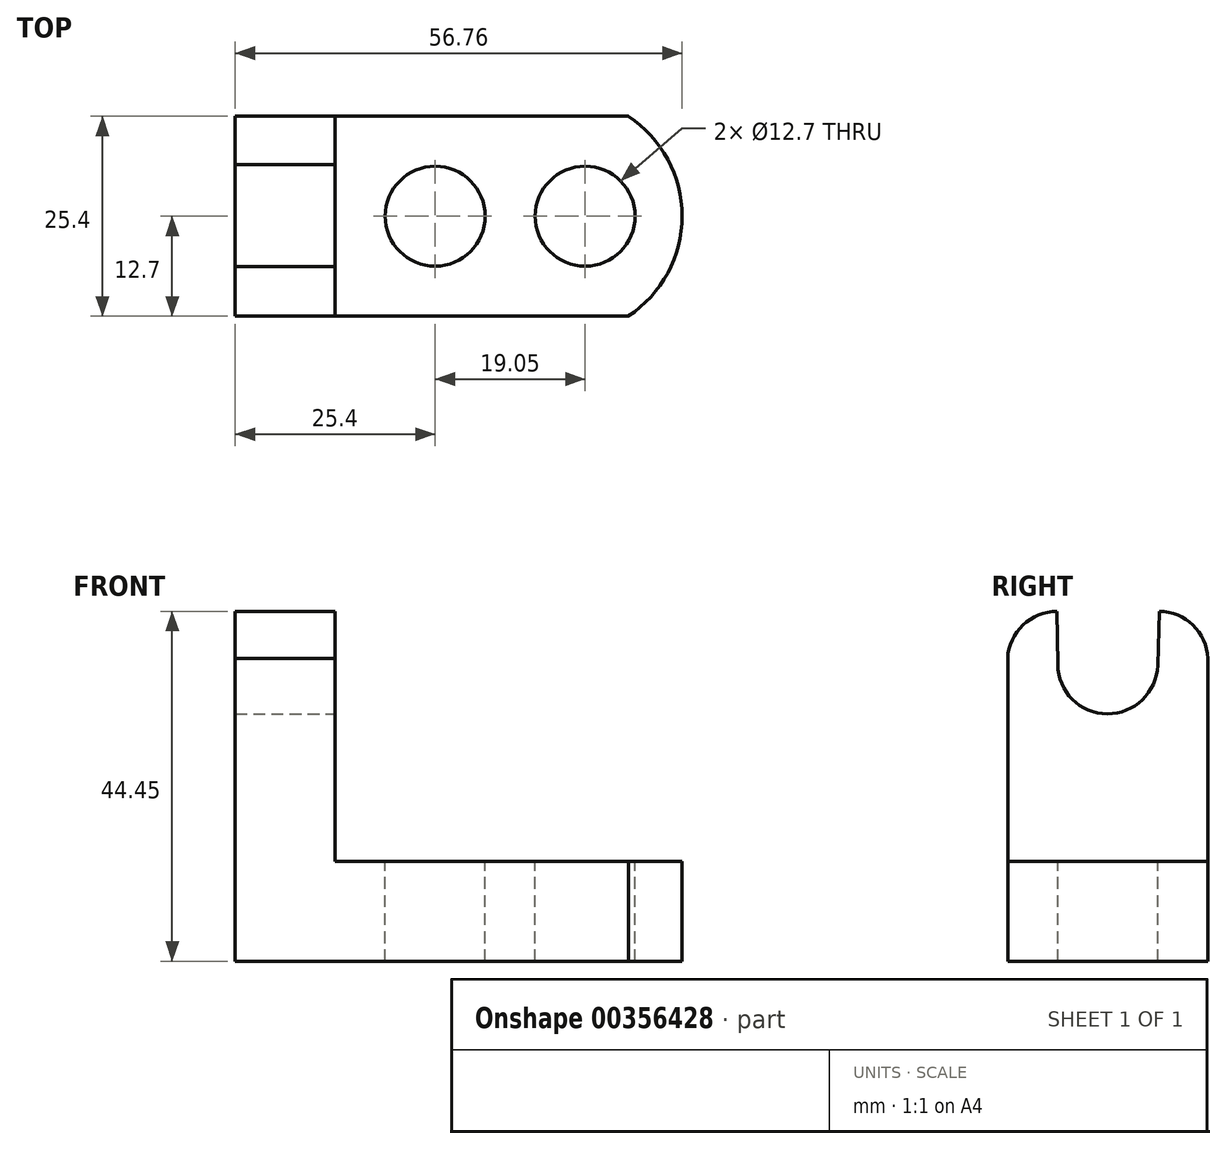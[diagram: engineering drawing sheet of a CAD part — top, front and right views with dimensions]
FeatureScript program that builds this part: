
annotation { "Feature Type Name" : "Feature", "Feature Type Description" : "" }
export const myFeature = defineFeature(function(context is Context, id is Id, definition is map)
    precondition{}
    {
        {
            var Q0;
            Q0=qCreatedBy(makeId("Front.planeOp"),FACE);
            var sketch = newSketch(context, id + "F0", { "sketchPlane" : qUnion([Q0])});
            skLineSegment(sketch, "E0", {"start": v(0, 44.45) * mm, "end": v(0, 0) * mm});
            skLineSegment(sketch, "E1", {"start": v(0, 0) * mm, "end": v(57.15, 0) * mm});
            skLineSegment(sketch, "E2", {"start": v(57.15, 0) * mm, "end": v(57.15, 44.45) * mm});
            skLineSegment(sketch, "E3", {"start": v(57.15, 44.45) * mm, "end": v(0, 44.45) * mm});
            skSolve(sketch);
        }
        {
            var Q0;
            Q0=makeQuery(id+"F0.imprint","IMPRINT",FACE,{"disambiguationData":[TD([[makeQuery(id+"F0.imprint","IMPRINT",EDGE,{"derivedFrom":sQuery(id+"F0.wireOp",EDGE,"E0")}),1.0]])]});
            extrude(context, id + "F1", {"entities" : qUnion([Q0]), "depth" : 25.4 * mm});
        }
        {
            var Q0;
            Q0=makeQuery(id+"F1.opExtrude","CAP_FACE",FACE,{"disambiguationData":[OSD([sQuery(id+"F0.wireOp",EDGE,"E0"),sQuery(id+"F0.wireOp",EDGE,"E1"),sQuery(id+"F0.wireOp",EDGE,"E2"),sQuery(id+"F0.wireOp",EDGE,"E3")])],"isStart":false});
            var sketch = newSketch(context, id + "F2", { "sketchPlane" : qUnion([Q0])});
            skLineSegment(sketch, "E4", {"start": v(12.7, 44.45) * mm, "end": v(12.7, 12.7) * mm});
            skLineSegment(sketch, "E5", {"start": v(12.7, 12.7) * mm, "end": v(57.15, 12.7) * mm});
            skSolve(sketch);
        }
        {
            var Q0;
            Q0 = qSketchRegion(id + "F2", true);
            var Q1;
            {var subQ0=sQuery(id+"F2.wireOp",EDGE,"E4");Q1=makeQuery(id+"F2.imprint","IMPRINT",FACE,{"disambiguationData":[TD([[makeQuery(id+"F2.imprint","IMPRINT",EDGE,{"derivedFrom":subQ0}),1.0]])]});}
            extrude(context, id + "F3", {"entities" : qUnion([Q0, Q1]), "operationType" : NewBodyOperationType.REMOVE, "oppositeDirection" : true, "depth" : 25.4 * mm});
        }
        {
            var Q0;
            Q0=makeQuery(id+"F3.boolean.opBoolean","COPY",FACE,{"derivedFrom":makeQuery(id+"F3.opExtrude","SWEPT_FACE",FACE,{"disambiguationData":[OSD([sQuery(id+"F2.wireOp",EDGE,"E4")])]})});
            var sketch = newSketch(context, id + "F4", { "sketchPlane" : qUnion([Q0])});
            skCircle(sketch, "E6", {"center": v(-12.7, 37.78) * mm, "radius": 6.35 * mm});
            skLineSegment(sketch, "E7", {"start": v(-19.05, 37.71) * mm, "end": v(-19.12, 44.45) * mm});
            skLineSegment(sketch, "E8", {"start": v(-19.12, 44.45) * mm, "end": v(-6.15, 44.45) * mm});
            skLineSegment(sketch, "E9", {"start": v(-6.15, 44.45) * mm, "end": v(-6.35, 37.6) * mm});
            skSolve(sketch);
        }
        {
            var Q0;
            {var subQ0=sQuery(id+"F4.wireOp",EDGE,"E7");Q0=makeQuery(id+"F4.imprint","IMPRINT",FACE,{"disambiguationData":[TD([[makeQuery(id+"F4.imprint","IMPRINT",EDGE,{"derivedFrom":subQ0}),-1.0]])]});}
            var Q1;
            {var subQ0=sQuery(id+"F4.wireOp",EDGE,"E6");var subQ1=makeQuery(id+"F4.imprint","INTERSECT",VERTEX,{"derivedFrom":[subQ0,sQuery(id+"F4.wireOp",EDGE,"E7")]});Q1=makeQuery(id+"F4.imprint","IMPRINT",FACE,{"disambiguationData":[TD([[makeQuery(id+"F4.imprint","IMPRINT",EDGE,{"disambiguationData":[TD([[subQ1,-1.0]])],"derivedFrom":subQ0}),1.0]])]});}
            extrude(context, id + "F5", {"entities" : qUnion([Q0, Q1]), "operationType" : NewBodyOperationType.REMOVE, "oppositeDirection" : true, "depth" : 25.4 * mm});
        }
        {
            var Q0;
            Q0=makeQuery(id+"F3.boolean.opBoolean","COPY",FACE,{"derivedFrom":makeQuery(id+"F3.opExtrude","SWEPT_FACE",FACE,{"disambiguationData":[OSD([sQuery(id+"F2.wireOp",EDGE,"E4")])]})});
            var sketch = newSketch(context, id + "F6", { "sketchPlane" : qUnion([Q0])});
            skArc(sketch, "E10", {"start": v(-19.12, 44.45) * mm, "mid": v(-23.46, 42.71) * mm, "end": v(-25.4, 38.47) * mm});
            skSolve(sketch);
        }
        {
            var Q0;
            Q0 = qSketchRegion(id + "F6", true);
            var Q1;
            {var subQ0=sQuery(id+"F6.wireOp",EDGE,"E10");Q1=makeQuery(id+"F6.imprint","IMPRINT",FACE,{"disambiguationData":[TD([[makeQuery(id+"F6.imprint","IMPRINT",EDGE,{"derivedFrom":subQ0}),-1.0]])]});}
            extrude(context, id + "F7", {"entities" : qUnion([Q0, Q1]), "operationType" : NewBodyOperationType.REMOVE, "oppositeDirection" : true, "depth" : 25.4 * mm});
        }
        {
            var Q0;
            Q0=makeQuery(id+"F3.boolean.opBoolean","COPY",FACE,{"derivedFrom":makeQuery(id+"F3.opExtrude","SWEPT_FACE",FACE,{"disambiguationData":[OSD([sQuery(id+"F2.wireOp",EDGE,"E4")])]})});
            var sketch = newSketch(context, id + "F8", { "sketchPlane" : qUnion([Q0])});
            skArc(sketch, "E11", {"start": v(0, 38.47) * mm, "mid": v(-1.86, 42.7) * mm, "end": v(-6.15, 44.45) * mm});
            skSolve(sketch);
        }
        {
            var Q0;
            Q0 = qSketchRegion(id + "F8", true);
            var Q1;
            {var subQ0=sQuery(id+"F8.wireOp",EDGE,"E11");Q1=makeQuery(id+"F8.imprint","IMPRINT",FACE,{"disambiguationData":[TD([[makeQuery(id+"F8.imprint","IMPRINT",EDGE,{"derivedFrom":subQ0}),-1.0]])]});}
            extrude(context, id + "F9", {"entities" : qUnion([Q0, Q1]), "operationType" : NewBodyOperationType.REMOVE, "oppositeDirection" : true, "depth" : 25.4 * mm});
        }
        {
            var Q0;
            Q0=makeQuery(id+"F3.boolean.opBoolean","COPY",FACE,{"derivedFrom":makeQuery(id+"F3.opExtrude","SWEPT_FACE",FACE,{"disambiguationData":[OSD([sQuery(id+"F2.wireOp",EDGE,"E5")])]})});
            var sketch = newSketch(context, id + "F10", { "sketchPlane" : qUnion([Q0])});
            skCircle(sketch, "E12", {"center": v(25.4, -12.7) * mm, "radius": 6.35 * mm});
            skCircle(sketch, "E13", {"center": v(44.45, -12.7) * mm, "radius": 6.35 * mm});
            skSolve(sketch);
        }
        {
            var Q0;
            Q0=makeQuery(id+"F10.imprint","IMPRINT",FACE,{"disambiguationData":[TD([[makeQuery(id+"F10.imprint","IMPRINT",EDGE,{"derivedFrom":sQuery(id+"F10.wireOp",EDGE,"E13")}),1.0]])]});
            var Q1;
            Q1=makeQuery(id+"F10.imprint","IMPRINT",FACE,{"disambiguationData":[TD([[makeQuery(id+"F10.imprint","IMPRINT",EDGE,{"derivedFrom":sQuery(id+"F10.wireOp",EDGE,"E12")}),1.0]])]});
            extrude(context, id + "F11", {"entities" : qUnion([Q0, Q1]), "operationType" : NewBodyOperationType.REMOVE, "oppositeDirection" : true, "depth" : 25.4 * mm});
        }
        {
            var Q0;
            Q0=makeQuery(id+"F3.boolean.opBoolean","COPY",FACE,{"derivedFrom":makeQuery(id+"F3.opExtrude","SWEPT_FACE",FACE,{"disambiguationData":[OSD([sQuery(id+"F2.wireOp",EDGE,"E5")])]})});
            var sketch = newSketch(context, id + "F12", { "sketchPlane" : qUnion([Q0])});
            skArc(sketch, "E14", {"start": v(49.92, -25.4) * mm, "mid": v(56.76, -12.7) * mm, "end": v(49.92, 0) * mm});
            skSolve(sketch);
        }
        {
            var Q0;
            Q0 = qSketchRegion(id + "F12", true);
            var Q1;
            {var subQ0=sQuery(id+"F12.wireOp",EDGE,"E14");Q1=makeQuery(id+"F12.imprint","IMPRINT",FACE,{"disambiguationData":[TD([[makeQuery(id+"F12.imprint","IMPRINT",EDGE,{"derivedFrom":subQ0}),-1.0]])]});}
            extrude(context, id + "F13", {"entities" : qUnion([Q0, Q1]), "operationType" : NewBodyOperationType.REMOVE, "oppositeDirection" : true, "depth" : 25.4 * mm});
        }
    });
